# Revit family: Siedzisko_prysznicowe_uchylne_stal_biala
name_source: partatom
category: Furniture
units: mm (PartAtom-declared; Revit-internal decimal feet)

## family parameters
Always vertical = Yes
Cut with Voids When Loaded = No
Host = Wall
Room Calculation Point = No
Shared = No

## types (1)
- S25KPU2SWB
    Color / Kolor = Farba epoksydowa biała
    Depth / Glebokosc = 460 mm  [stored 1.50919 ft]
    Description = Siedzisko prysznicowe uchylne to krzesełko łazienkowe przeznaczone do toalet dla niepełnosprawnych. Montuje się je naściennie pod prysznicem w celu wsparcia osób z dysfunkcjami ruchowymi. Dzięki niemu użytkownicy są bardziej samodzielni, czują się bezpieczniej i mogą w wygodniejszy sposób korzystać z prysznica. Taboret łazienkowy wykonany jest ze stali węglowej, pomalowanej na biało. Możliwość złożenia go pozwala zaoszczędzić miejsce w czasie, gdy nie jest on użytkowany. Uniwersalne, odporne na uszkodzenia, stabilne i funkcjonalne siedzisko umożliwia skuteczne dostosowanie toalety do potrzeb osób niepełnosprawnych.
    Height / Wysokosc = 150 mm  [stored 0.492126 ft]
    Manufacturer = FANECO.com
    Manufacturer code / Kod producenta = 5901764295297
    Material = Farba epoksydowa biała
    Material finish / Wykonczenie = Stal węglowa
    Product code / Kod produktu = S25KPU2SWB
    Type Comments = Siedzisko prysznicowe uchylne stal biała
    URL = https://faneco.com
    Weight / Waga = 7.2 kg
    Width / Szerokosc = 440 mm  [stored 1.44357 ft]

note: [stored X ft] marks values corroborated as IEEE doubles in the binary element streams (Revit-internal decimal feet)

## geometry (parser evidence)
native form markers: Sweep x9
no freeform markers — native parametric forms only
